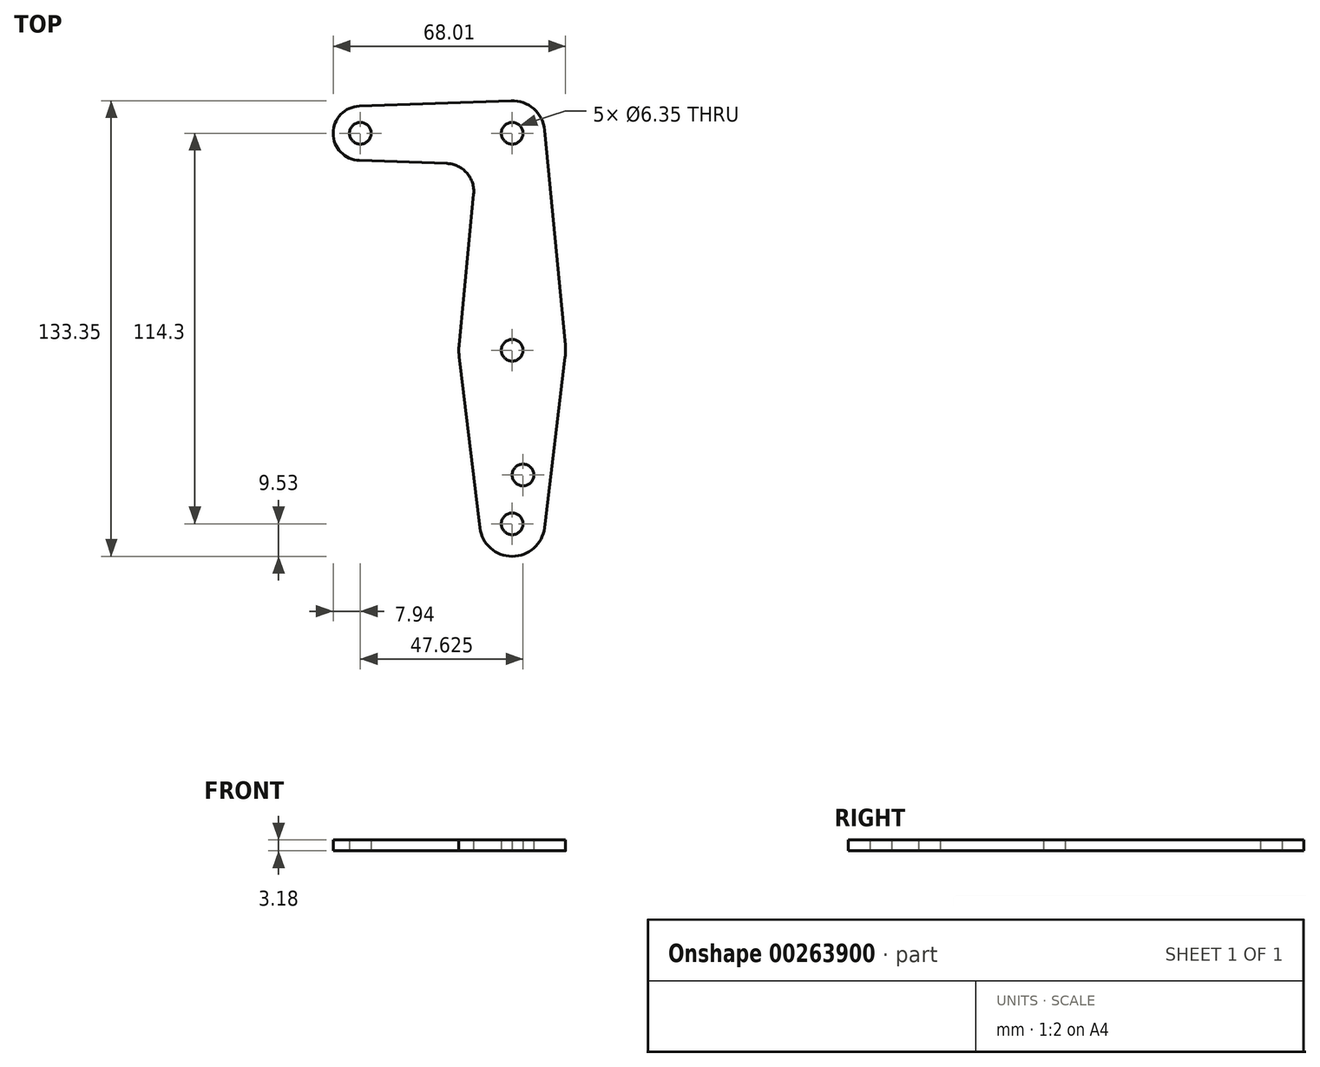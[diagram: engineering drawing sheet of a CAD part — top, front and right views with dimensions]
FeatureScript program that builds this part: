
annotation { "Feature Type Name" : "Feature", "Feature Type Description" : "" }
export const myFeature = defineFeature(function(context is Context, id is Id, definition is map)
    precondition{}
    {
        {
            var Q0;
            Q0=qCreatedBy(makeId("Top.planeOp"),FACE);
            var sketch = newSketch(context, id + "F0", { "sketchPlane" : qUnion([Q0])});
            skCircle(sketch, "E0", {"center": v(-44.45, 0) * mm, "radius": 3.18 * mm});
            skCircle(sketch, "E1", {"center": v(0, 0) * mm, "radius": 3.18 * mm});
            skCircle(sketch, "E2", {"center": v(0, -63.5) * mm, "radius": 3.18 * mm});
            skCircle(sketch, "E3", {"center": v(0, -114.3) * mm, "radius": 3.18 * mm});
            skCircle(sketch, "E4", {"center": v(3.17, -100.01) * mm, "radius": 3.18 * mm});
            skCircle(sketch, "E5", {"center": v(-44.45, 0) * mm, "radius": 7.94 * mm});
            skCircle(sketch, "E6", {"center": v(0, -63.5) * mm, "radius": 15.62 * mm});
            skCircle(sketch, "E7", {"center": v(0, -114.3) * mm, "radius": 9.53 * mm});
            skPoint(sketch, "E8.orphan", {"position": v(0, 16.2) * mm});
            skLineSegment(sketch, "E9", {"start": v(15.5, -65.37) * mm, "end": v(9.46, -115.44) * mm});
            skLineSegment(sketch, "E10", {"start": v(-9.46, -115.44) * mm, "end": v(-15.5, -65.37) * mm});
            skCircle(sketch, "E11", {"center": v(0, 0) * mm, "radius": 9.53 * mm});
            skLineSegment(sketch, "E12", {"start": v(9.48, 0.91) * mm, "end": v(15.55, -62) * mm});
            skLineSegment(sketch, "E13", {"start": v(-0.34, 9.52) * mm, "end": v(-44.73, 7.93) * mm});
            skPoint(sketch, "E14.endSnap0", {"position": v(12.51, -30.54) * mm});
            skPoint(sketch, "E15.orphan", {"position": v(587.96, -30.54) * mm});
            skLineSegment(sketch, "E16", {"start": v(-9.48, 0.91) * mm, "end": v(-15.55, -62) * mm});
            skLineSegment(sketch, "E17", {"start": v(-44.73, -7.93) * mm, "end": v(-0.34, -9.52) * mm});
            skSolve(sketch);
        }
        {
            var Q0;
            Q0 = qSketchRegion(id + "F0", true);
            extrude(context, id + "F1", {"entities" : qUnion([Q0]), "depth" : 3.17 * mm});
        }
        {
            var Q0;
            Q0=makeQuery(id+"F1.opExtrude","SWEPT_EDGE",EDGE,{"disambiguationData":[OSD([sQuery(id+"F0.wireOp",EDGE,"E16"),sQuery(id+"F0.wireOp",EDGE,"E17")])]});
            fillet(context, id + "F2", {"entities" : qUnion([Q0]), "radius" : 8.2 * mm, "tangentPropagation" : true, "allowEdgeOverflow" : false});
        }
    });
